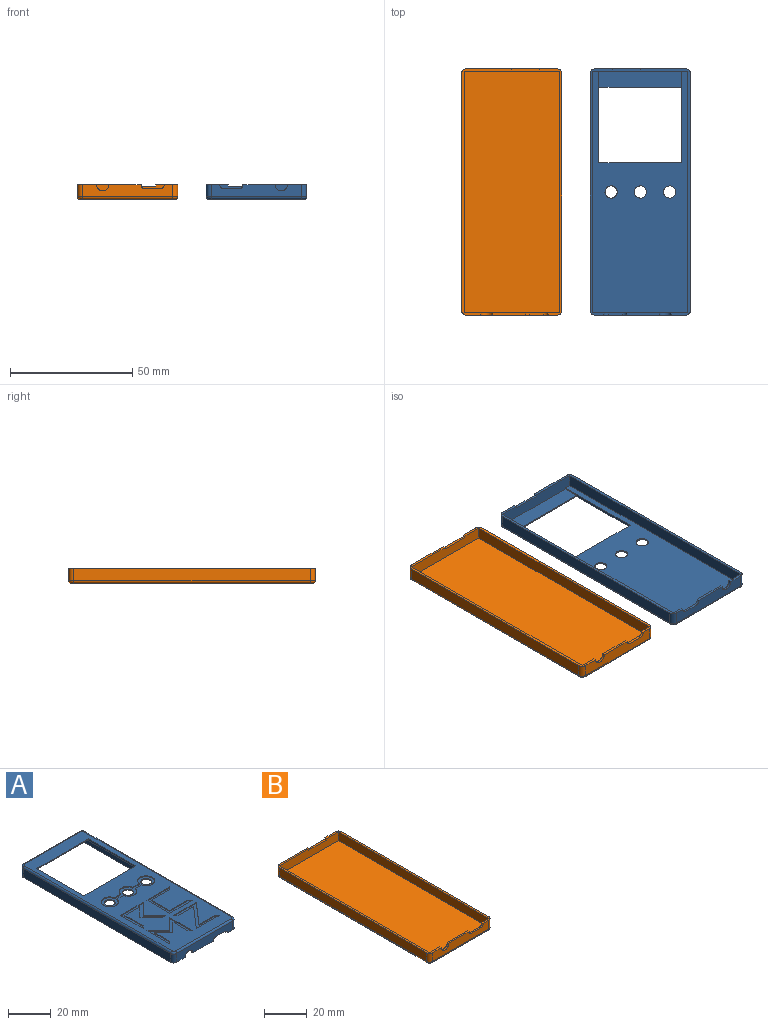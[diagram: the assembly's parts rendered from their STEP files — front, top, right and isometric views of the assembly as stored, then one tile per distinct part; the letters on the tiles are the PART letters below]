
ASSEMBLY  parts=2 mates=1
PART A: 89 faces, bbox 41.3x101.3x6 mm
  f0: plane 37x5mm, normal (0,1,0), area 176.4mm2, adj f12,f18,f20,f83,f84,f85,f86,f87
  f1: plane 39x5.5mm, normal (0,-1,0), area 203.4mm2, adj f23,f24,f26,f27,f28,f29,f83,f84
  f2: plane 37x5mm, normal (0,-1,0), area 159.9mm2, adj f13,f16,f22,f79,f80,f81,f82,f86
  f3: plane 39x5mm, normal (0,1,0), area 169.9mm2, adj f26,f27,f28,f79,f80,f81,f82,f86
  f4: plane 99x39mm, normal (0,0,1), area 2382.7mm2, adj f8,f11,f12,f13,f14,f15,f17,f19
  f5: cylinder r=2.5mm len=5mm, axis (0,0,1), area 7.9mm2, adj f26,f30
  f6: cylinder r=2.5mm len=5mm, axis (0,0,1), area 7.9mm2, adj f26,f30
  f7: cylinder r=2.5mm len=5mm, axis (0,0,1), area 7.9mm2, adj f26,f30
  f8: plane 34x0.5mm, normal (0,-1,0), area 17mm2, adj f4,f23,f24,f29
  f9: plane 97x5mm, normal (1,0,0), area 485mm2, adj f11,f20,f22,f86
  f10: plane 97x5mm, normal (-1,0,0), area 485mm2, adj f14,f16,f18,f87
  f11: cylinder r=1mm len=97mm, axis (0,-1,0), area 152.4mm2, adj f4,f9,f19,f21
  f12: cylinder r=1mm len=37mm, axis (1,0,0), area 58.1mm2, adj f0,f4,f17,f19
  f13: cylinder r=1mm len=37mm, axis (-1,0,0), area 58.1mm2, adj f2,f4,f15,f21
  f14: cylinder r=1mm len=97mm, axis (0,1,0), area 152.4mm2, adj f4,f10,f15,f17
  f15: torus R=1mm, axis (0,0,1), area 4mm2, adj f4,f13,f14,f16
  f16: cylinder r=2mm len=5mm, axis (0,0,1), area 15.7mm2, adj f2,f10,f15,f87
  f17: torus R=1mm, axis (0,0,1), area 4mm2, adj f4,f12,f14,f18
  f18: cylinder r=2mm len=5mm, axis (0,0,-1), area 15.7mm2, adj f0,f10,f17,f87
  f19: torus R=1mm, axis (0,0,1), area 4mm2, adj f4,f11,f12,f20
  f20: cylinder r=2mm len=5mm, axis (0,0,1), area 15.7mm2, adj f0,f9,f19,f86
  f21: torus R=1mm, axis (0,0,1), area 4mm2, adj f4,f11,f13,f22
  f22: cylinder r=2mm len=5mm, axis (0,0,-1), area 15.7mm2, adj f2,f9,f21,f86
  f23: plane 37.5x1mm, normal (-1,0,0), area 34.2mm2, adj f1,f4,f8,f25,f26,f29
  f24: plane 37.5x1mm, normal (1,0,0), area 34.2mm2, adj f1,f4,f8,f25,f26,f29
  f25: plane 34x1mm, normal (0,1,0), area 34mm2, adj f4,f23,f24,f26
  f26: plane 99x39mm, normal (0,0,-1), area 2527.1mm2, adj f1,f3,f5,f6,f7,f23,f24,f25
  f27: plane 99x5mm, normal (-1,0,0), area 495mm2, adj f1,f3,f26,f86
  f28: plane 99x5mm, normal (1,0,0), area 495mm2, adj f1,f3,f26,f87
  f29: plane 34x6.5mm, normal (0,0,-1), area 221mm2, adj f1,f8,f23,f24
  f30: plane 32x8mm, normal (0,0,1), area 104mm2, adj f5,f6,f7,f31,f32,f33,f34,f35
  f31: plane 4.14x0.5mm, normal (0,1,0), area 2.1mm2, adj f4,f30,f32,f38
  f32: cylinder r=4mm len=7.86mm, axis (0,0,1), area 5.5mm2, adj f4,f30,f31,f33
  f33: plane 4.14x0.5mm, normal (0,1,0), area 2.1mm2, adj f4,f30,f32,f34
  f34: cylinder r=4mm len=8mm, axis (0,0,1), area 11.8mm2, adj f4,f30,f33,f35
  f35: plane 4.14x0.5mm, normal (0,-1,0), area 2.1mm2, adj f4,f30,f34,f36
  f36: cylinder r=4mm len=7.86mm, axis (0,0,1), area 5.5mm2, adj f4,f30,f35,f37
  f37: plane 4.14x0.5mm, normal (0,-1,0), area 2.1mm2, adj f4,f30,f36,f38
  f38: cylinder r=4mm len=8mm, axis (0,0,1), area 11.8mm2, adj f4,f30,f31,f37
  f39: plane 15x0.5mm, normal (1,0,0), area 7.5mm2, adj f4,f40,f48,f49
  f40: plane 1.5x1.5mm, normal (-0.71,0.71,0), area 1.1mm2, adj f4,f39,f41,f49
  f41: plane 12x0.5mm, normal (-1,0,0), area 6mm2, adj f4,f40,f42,f49
  f42: plane 9.88x0.5mm, normal (0,1,0), area 4.9mm2, adj f4,f41,f43,f49
  f43: plane 6x6mm, normal (0.71,-0.71,0), area 4.2mm2, adj f4,f42,f44,f49
  f44: plane 7.5x7.5mm, normal (0.71,0.71,0), area 5.3mm2, adj f4,f43,f45,f49
  f45: plane 2.12x0.5mm, normal (0,1,0), area 1.1mm2, adj f4,f44,f46,f49
  f46: plane 7.5x7.5mm, normal (-0.71,-0.71,0), area 5.3mm2, adj f4,f45,f47,f49
  f47: plane 7.5x7.5mm, normal (-0.71,0.71,0), area 5.3mm2, adj f4,f46,f48,f49
  f48: plane 15x0.5mm, normal (0,-1,0), area 7.5mm2, adj f4,f39,f47,f49
  f49: plane 15x15mm, normal (0,0,1), area 69.1mm2, adj f39,f40,f41,f42,f43,f44,f45,f46
  f50: plane 15x0.5mm, normal (0,1,0), area 7.5mm2, adj f4,f51,f57,f58
  f51: plane 1.5x1.5mm, normal (-0.71,-0.71,0), area 1.1mm2, adj f4,f50,f52,f58
  f52: plane 10.21x0.5mm, normal (0,-1,0), area 5.1mm2, adj f4,f51,f53,f58
  f53: plane 13.5x11.71mm, normal (-0.76,0.66,0), area 8.9mm2, adj f4,f52,f54,f58
  f54: plane 15x0.5mm, normal (0,-1,0), area 7.5mm2, adj f4,f53,f55,f58
  f55: plane 1.5x1.5mm, normal (0.71,0.71,0), area 1.1mm2, adj f4,f54,f56,f58
  f56: plane 10.21x0.5mm, normal (0,1,0), area 5.1mm2, adj f4,f55,f57,f58
  f57: plane 13.5x11.71mm, normal (0.76,-0.66,0), area 8.9mm2, adj f4,f50,f56,f58
  f58: plane 15x15mm, normal (0,0,1), area 64.6mm2, adj f50,f51,f52,f53,f54,f55,f56,f57
  f59: plane 15x0.5mm, normal (1,0,0), area 7.5mm2, adj f4,f60,f68,f69
  f60: plane 1.5x1.5mm, normal (-0.71,0.71,0), area 1.1mm2, adj f4,f59,f61,f69
  f61: plane 9.88x0.5mm, normal (-1,0,0), area 4.9mm2, adj f4,f60,f62,f69
  f62: plane 6x6mm, normal (0.71,0.71,0), area 4.2mm2, adj f4,f61,f63,f69
  f63: plane 6x6mm, normal (-0.71,0.71,0), area 4.2mm2, adj f4,f62,f64,f69
  f64: plane 9.88x0.5mm, normal (1,0,0), area 4.9mm2, adj f4,f63,f65,f69
  f65: plane 1.5x1.5mm, normal (0.71,0.71,0), area 1.1mm2, adj f4,f64,f66,f69
  f66: plane 15x0.5mm, normal (-1,0,0), area 7.5mm2, adj f4,f65,f67,f69
  f67: plane 7.5x7.5mm, normal (0.71,-0.71,0), area 5.3mm2, adj f4,f66,f68,f69
  f68: plane 7.5x7.5mm, normal (-0.71,-0.71,0), area 5.3mm2, adj f4,f59,f67,f69
  f69: plane 15x15mm, normal (0,0,1), area 66mm2, adj f59,f60,f61,f62,f63,f64,f65,f66
  f70: plane 15x0.5mm, normal (0,1,0), area 7.5mm2, adj f4,f71,f77,f78
  f71: plane 1.5x1.5mm, normal (-0.71,-0.71,0), area 1.1mm2, adj f4,f70,f72,f78
  f72: plane 12x0.5mm, normal (0,-1,0), area 6mm2, adj f4,f71,f73,f78
  f73: plane 12x0.5mm, normal (-1,0,0), area 6mm2, adj f4,f72,f74,f78
  f74: plane 12x0.5mm, normal (0,1,0), area 6mm2, adj f4,f73,f75,f78
  f75: plane 1.5x1.5mm, normal (-0.71,0.71,0), area 1.1mm2, adj f4,f74,f76,f78
  f76: plane 15x0.5mm, normal (0,-1,0), area 7.5mm2, adj f4,f75,f77,f78
  f77: plane 15x0.5mm, normal (1,0,0), area 7.5mm2, adj f4,f70,f76,f78
  f78: plane 15x15mm, normal (0,0,1), area 60.8mm2, adj f70,f71,f72,f73,f74,f75,f76,f77
  f79: plane 6x1mm, normal (0,0,-1), area 6mm2, adj f2,f3,f80,f81
  f80: cylinder r=1.75mm len=1.75mm, axis (0,-1,0), area 2.7mm2, adj f2,f3,f79,f88
  f81: cylinder r=1.75mm len=1.75mm, axis (0,-1,0), area 2.7mm2, adj f2,f3,f79,f86
  f82: cylinder r=2.5mm len=5mm, axis (0,-1,0), area 7.9mm2, adj f2,f3,f87,f88
  f83: plane 1x0.75mm, normal (1,0,0), area 0.8mm2, adj f0,f1,f84,f87
  f84: plane 11.5x1mm, normal (0,0,-1), area 11.5mm2, adj f0,f1,f83,f85
  f85: plane 1x0.75mm, normal (-1,0,0), area 0.8mm2, adj f0,f1,f84,f86
  f86: plane 101x9mm, normal (0,0,-1), area 111.8mm2, adj f0,f1,f2,f3,f9,f20,f22,f27
  f87: plane 101x20.5mm, normal (0,0,-1), area 125.5mm2, adj f0,f1,f2,f3,f10,f16,f18,f28
  f88: plane 13.25x1mm, normal (0,0,-1), area 13.3mm2, adj f2,f3,f80,f82
PART B: 32 faces, bbox 41.3x101.3x6 mm
  f0: plane 13.25x1mm, normal (0,0,1), area 13.3mm2, adj f19,f20,f23,f27
  f1: plane 99x39mm, normal (0,0,-1), area 3860.1mm2, adj f2,f3,f4,f5,f6,f7,f8,f9
  f2: cylinder r=1mm len=37mm, axis (-1,0,0), area 58.1mm2, adj f1,f7,f8,f29
  f3: cylinder r=1mm len=37mm, axis (1,0,0), area 58.1mm2, adj f1,f6,f9,f27
  f4: cylinder r=1mm len=97mm, axis (0,1,0), area 152.4mm2, adj f1,f8,f9,f26
  f5: cylinder r=1mm len=97mm, axis (0,-1,0), area 152.4mm2, adj f1,f6,f7,f17
  f6: torus R=1mm, axis (0,0,1), area 4mm2, adj f1,f3,f5,f15
  f7: torus R=1mm, axis (0,0,1), area 4mm2, adj f1,f2,f5,f16
  f8: torus R=1mm, axis (0,0,1), area 4mm2, adj f1,f2,f4,f25
  f9: torus R=1mm, axis (0,0,1), area 4mm2, adj f1,f3,f4,f24
  f10: plane 99x39mm, normal (0,0,1), area 3861mm2, adj f21,f22,f23,f28
  f11: plane 6x1mm, normal (0,0,1), area 6mm2, adj f18,f19,f23,f27
  f12: plane 11.5x1mm, normal (0,0,1), area 11.5mm2, adj f13,f14,f28,f29
  f13: plane 1x0.75mm, normal (1,0,0), area 0.7mm2, adj f12,f28,f29,f31
  f14: plane 1x0.75mm, normal (-1,0,0), area 0.7mm2, adj f12,f28,f29,f30
  f15: cylinder r=2mm len=5mm, axis (0,0,1), area 15.7mm2, adj f6,f17,f27,f31
  f16: cylinder r=2mm len=5mm, axis (0,0,-1), area 15.7mm2, adj f7,f17,f29,f31
  f17: plane 97x5mm, normal (-1,0,0), area 485mm2, adj f5,f15,f16,f31
  f18: cylinder r=1.75mm len=1.75mm, axis (0,-1,0), area 2.7mm2, adj f11,f23,f27,f30
  f19: cylinder r=1.75mm len=1.75mm, axis (0,-1,0), area 2.7mm2, adj f0,f11,f23,f27
  f20: cylinder r=2.5mm len=5mm, axis (0,-1,0), area 7.9mm2, adj f0,f23,f27,f31
  f21: plane 99x5mm, normal (1,0,0), area 495mm2, adj f10,f23,f28,f31
  f22: plane 99x5mm, normal (-1,0,0), area 495mm2, adj f10,f23,f28,f30
  f23: plane 39x5mm, normal (0,1,0), area 169.9mm2, adj f0,f10,f11,f18,f19,f20,f21,f22
  f24: cylinder r=2mm len=5mm, axis (0,0,-1), area 15.7mm2, adj f9,f26,f27,f30
  f25: cylinder r=2mm len=5mm, axis (0,0,1), area 15.7mm2, adj f8,f26,f29,f30
  f26: plane 97x5mm, normal (1,0,0), area 485mm2, adj f4,f24,f25,f30
  f27: plane 37x5mm, normal (0,-1,0), area 159.9mm2, adj f0,f3,f11,f15,f18,f19,f20,f24
  f28: plane 39x5mm, normal (0,-1,0), area 186.4mm2, adj f10,f12,f13,f14,f21,f22,f30,f31
  f29: plane 37x5mm, normal (0,1,0), area 176.4mm2, adj f2,f12,f13,f14,f16,f25,f30,f31
  f30: plane 101x9mm, normal (0,0,1), area 111.8mm2, adj f14,f18,f22,f23,f24,f25,f26,f27
  f31: plane 101x20.5mm, normal (0,0,1), area 125.5mm2, adj f13,f15,f16,f17,f20,f21,f23,f27
PLACE A rot(axis=(0,1,0),180deg) t=(32.76,-50,7.5)mm
PLACE B t=(-20,-50,7.5)mm
MATE planar A.f0 <-> B.f29  axis (0,1,0) through (33.04,0.5,4.9)mm
